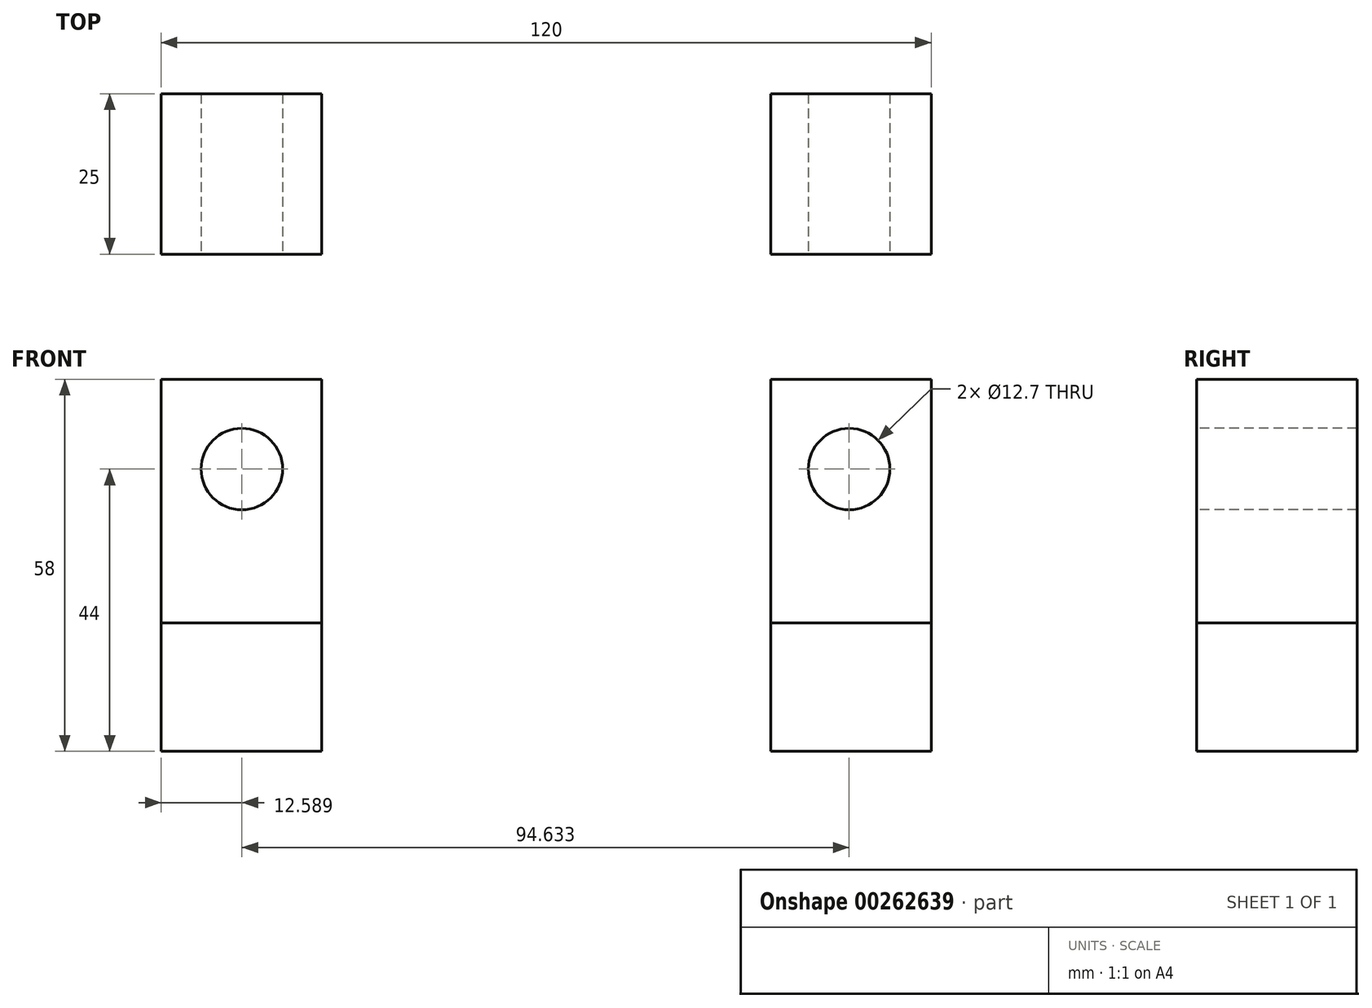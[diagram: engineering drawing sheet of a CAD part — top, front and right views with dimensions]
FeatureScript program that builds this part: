
annotation { "Feature Type Name" : "Feature", "Feature Type Description" : "" }
export const myFeature = defineFeature(function(context is Context, id is Id, definition is map)
    precondition{}
    {
        {
            var Q0;
            Q0=qCreatedBy(makeId("Top.planeOp"),FACE);
            var sketch = newSketch(context, id + "F0", { "sketchPlane" : qUnion([Q0])});
            skLineSegment(sketch, "E0", {"start": v(-55, 29.91) * mm, "end": v(65, 29.91) * mm});
            skLineSegment(sketch, "E1", {"start": v(65, 29.91) * mm, "end": v(65, 4.91) * mm});
            skLineSegment(sketch, "E2", {"start": v(65, 4.91) * mm, "end": v(27, 4.91) * mm});
            skLineSegment(sketch, "E3", {"start": v(27, 4.91) * mm, "end": v(27, -28.04) * mm});
            skLineSegment(sketch, "E4", {"start": v(27, -28.04) * mm, "end": v(-17, -28.04) * mm});
            skLineSegment(sketch, "E5", {"start": v(-17, -28.04) * mm, "end": v(-17, 4.91) * mm});
            skLineSegment(sketch, "E6", {"start": v(-17, 4.91) * mm, "end": v(-55, 4.91) * mm});
            skLineSegment(sketch, "E7", {"start": v(-55, 4.91) * mm, "end": v(-55, 29.91) * mm});
            skLineSegment(sketch, "E8", {"start": v(65, 29.91) * mm, "end": v(40, 29.91) * mm});
            skLineSegment(sketch, "E9", {"start": v(40, 29.91) * mm, "end": v(40, 4.91) * mm});
            skLineSegment(sketch, "E10", {"start": v(-55, 29.91) * mm, "end": v(-30, 29.91) * mm});
            skLineSegment(sketch, "E11", {"start": v(-30, 29.91) * mm, "end": v(-30, 4.91) * mm});
            skCircle(sketch, "E12", {"center": v(5, -11.57) * mm, "radius": 9.43 * mm});
            skSolve(sketch);
        }
        {
            var Q0;
            {var subQ0=sQuery(id+"F0.wireOp",EDGE,"E7");Q0=makeQuery(id+"F0.imprint","IMPRINT",FACE,{"disambiguationData":[TD([[makeQuery(id+"F0.imprint","IMPRINT",EDGE,{"derivedFrom":subQ0}),-1.0]])]});}
            var Q1;
            {var subQ0=sQuery(id+"F0.wireOp",EDGE,"E1");Q1=makeQuery(id+"F0.imprint","IMPRINT",FACE,{"disambiguationData":[TD([[makeQuery(id+"F0.imprint","IMPRINT",EDGE,{"derivedFrom":subQ0}),-1.0]])]});}
            extrude(context, id + "F1", {"entities" : qUnion([Q0, Q1]), "depth" : 58 * mm});
        }
        {
            var Q0;
            Q0=makeQuery(id+"F0.imprint","IMPRINT",FACE,{"disambiguationData":[TD([[makeQuery(id+"F0.imprint","IMPRINT",EDGE,{"derivedFrom":sQuery(id+"F0.wireOp",EDGE,"E0")}),-1.0]])]});
            extrude(context, id + "F2", {"entities" : qUnion([Q0]), "depth" : 20 * mm});
        }
        {
            var Q0;
            Q0=qCreatedBy(makeId("Front.planeOp"),FACE);
            var sketch = newSketch(context, id + "F3", { "sketchPlane" : qUnion([Q0])});
            skLineSegment(sketch, "E13", {"start": v(-54.92, 44) * mm, "end": v(-54.92, 0) * mm});
            skLineSegment(sketch, "E14", {"start": v(-54.92, 44) * mm, "end": v(-42.42, 44) * mm});
            skLineSegment(sketch, "E15", {"start": v(64.71, 44) * mm, "end": v(64.71, 0) * mm});
            skLineSegment(sketch, "E16", {"start": v(64.71, 44) * mm, "end": v(52.21, 44) * mm});
            skCircle(sketch, "E17", {"center": v(52.21, 44) * mm, "radius": 6 * mm});
            skCircle(sketch, "E18", {"center": v(-42.42, 44) * mm, "radius": 6 * mm});
            skSolve(sketch);
        }
        {
            var Q0;
            Q0=sQuery(id+"F3.wireOp",VERTEX,"E18.center");
            var Q1;
            Q1=sQuery(id+"F3.wireOp",VERTEX,"E17.center");
            var Q2;
            Q2=makeQuery(id+"F1.opExtrude","SWEPT_BODY",BODY,{"disambiguationData":[OSD([sQuery(id+"F0.wireOp",EDGE,"E6"),sQuery(id+"F0.wireOp",EDGE,"E7"),sQuery(id+"F0.wireOp",EDGE,"E10"),sQuery(id+"F0.wireOp",EDGE,"E11")])]});
            var Q3;
            Q3=makeQuery(id+"F1.opExtrude","SWEPT_BODY",BODY,{"disambiguationData":[OSD([sQuery(id+"F0.wireOp",EDGE,"E1"),sQuery(id+"F0.wireOp",EDGE,"E2"),sQuery(id+"F0.wireOp",EDGE,"E8"),sQuery(id+"F0.wireOp",EDGE,"E9")])]});
            hole(context, id + "F4", {"style" : HoleStyle.SIMPLE, "endStyle" : HoleEndStyle.THROUGH, "holeDiameter" : 12.7 * mm, "tappedDepth" : 12.7 * mm, "tapClearance" : 3, "locations" : qUnion([Q0, Q1]), "scope" : qUnion([Q2, Q3])});
        }
    });
